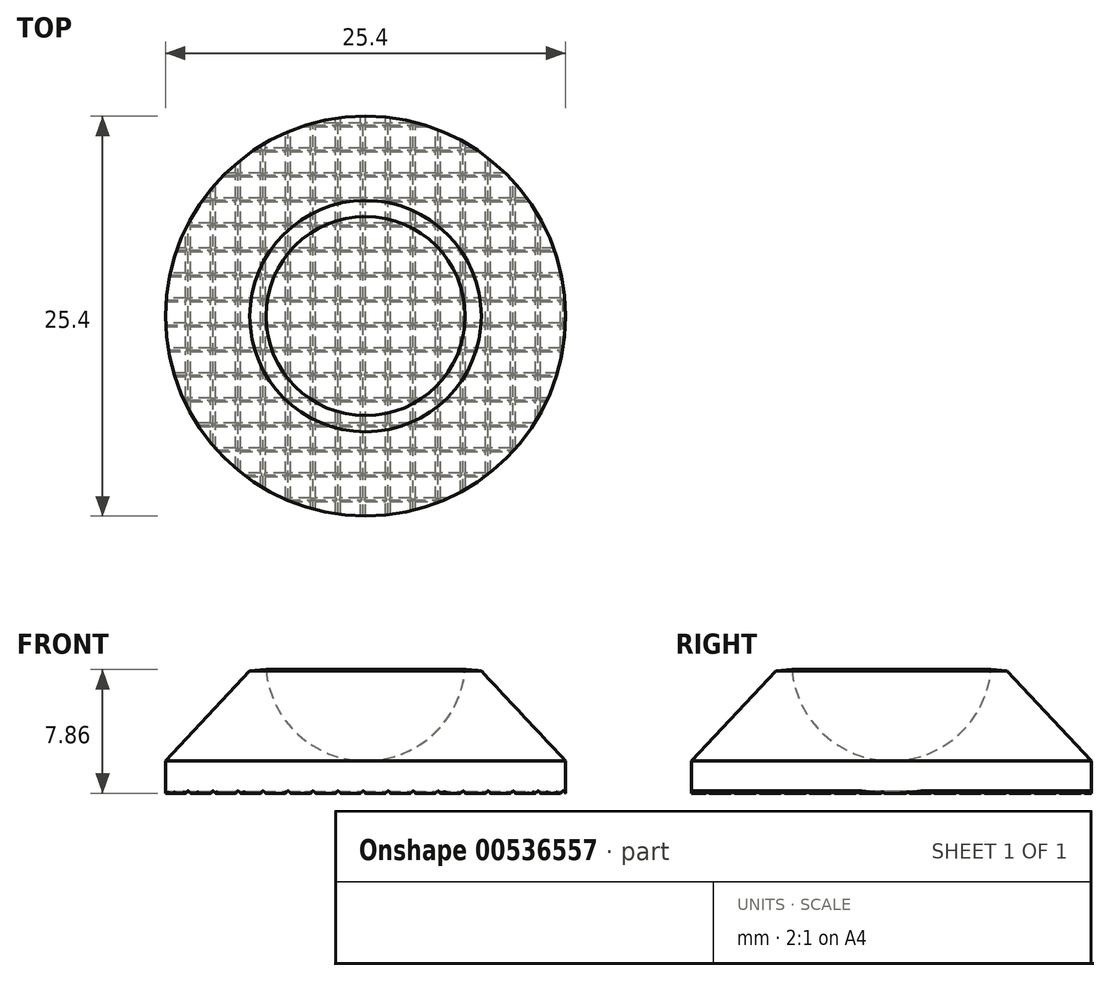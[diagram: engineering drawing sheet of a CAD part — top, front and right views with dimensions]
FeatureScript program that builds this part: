
annotation { "Feature Type Name" : "Feature", "Feature Type Description" : "" }
export const myFeature = defineFeature(function(context is Context, id is Id, definition is map)
    precondition{}
    {
        {
            var Q0;
            Q0=qCreatedBy(makeId("Front.planeOp"),FACE);
            var sketch = newSketch(context, id + "F0", { "sketchPlane" : qUnion([Q0])});
            skLineSegment(sketch, "E0", {"start": v(0, 0) * mm, "end": v(12.7, 0) * mm});
            skLineSegment(sketch, "E1", {"start": v(12.7, 0) * mm, "end": v(12.7, 2.06) * mm});
            skLineSegment(sketch, "E2", {"start": v(12.7, 2.06) * mm, "end": v(6.75, 8.41) * mm, "construction": true});
            skLineSegment(sketch, "E3", {"start": v(6.75, 8.41) * mm, "end": v(6.35, 8.41) * mm});
            skLineSegment(sketch, "E4", {"start": v(0, 0) * mm, "end": v(0, 2.06) * mm});
            skLineSegment(sketch, "E5", {"start": v(6.35, 8.41) * mm, "end": v(0, 8.41) * mm, "construction": true});
            skLineSegment(sketch, "E6", {"start": v(0, 8.41) * mm, "end": v(0, 2.06) * mm, "construction": true});
            skArc(sketch, "E7", {"start": v(0, 2.06) * mm, "mid": v(4.5, 3.92) * mm, "end": v(6.35, 8.41) * mm, "construction": true});
            skLineSegment(sketch, "E8", {"start": v(0, 2.06) * mm, "end": v(12.7, 2.06) * mm, "construction": true});
            skLineSegment(sketch, "E9", {"start": v(0, 8.41) * mm, "end": v(7.35, 7.77) * mm, "construction": true});
            skLineSegment(sketch, "E10", {"start": v(7.35, 7.77) * mm, "end": v(12.7, 2.06) * mm});
            skArc(sketch, "E11", {"start": v(0, 2.06) * mm, "mid": v(4.29, 3.73) * mm, "end": v(6.33, 7.86) * mm});
            skLineSegment(sketch, "E12", {"start": v(7.35, 7.77) * mm, "end": v(6.33, 7.86) * mm});
            skSolve(sketch);
        }
        {
            var Q0;
            Q0=qSketchRegion(id+"F0",true);
            var Q1;
            Q1=sQuery(id+"F0.wireOp",EDGE,"E6");
            revolve(context, id + "F1", {"entities" : qUnion([Q0]), "axis" : qUnion([Q1]), "revolveType" : RevolveType.FULL});
        }
        {
            var Q0;
            Q0=qCreatedBy(makeId("Front.planeOp"),FACE);
            var sketch = newSketch(context, id + "F2", { "sketchPlane" : qUnion([Q0])});
            skLineSegment(sketch, "E13", {"start": v(-12.7, 0) * mm, "end": v(-12.86, 0.16) * mm});
            skLineSegment(sketch, "E14", {"start": v(-12.86, 0.16) * mm, "end": v(-13.02, 0) * mm});
            skLineSegment(sketch, "E15", {"start": v(-13.02, 0) * mm, "end": v(-12.7, 0) * mm});
            skLineSegment(sketch, "E16.1.0.0", {"start": v(-11.11, 0) * mm, "end": v(-11.27, 0.16) * mm});
            skLineSegment(sketch, "E16.1.0.1", {"start": v(-11.27, 0.16) * mm, "end": v(-11.43, 0) * mm});
            skLineSegment(sketch, "E16.1.0.2", {"start": v(-11.43, 0) * mm, "end": v(-11.11, 0) * mm});
            skLineSegment(sketch, "E16.2.0.0", {"start": v(-9.53, 0) * mm, "end": v(-9.68, 0.16) * mm});
            skLineSegment(sketch, "E16.2.0.1", {"start": v(-9.68, 0.16) * mm, "end": v(-9.84, 0) * mm});
            skLineSegment(sketch, "E16.2.0.2", {"start": v(-9.84, 0) * mm, "end": v(-9.53, 0) * mm});
            skLineSegment(sketch, "E16.3.0.0", {"start": v(-7.94, 0) * mm, "end": v(-8.1, 0.16) * mm});
            skLineSegment(sketch, "E16.3.0.1", {"start": v(-8.1, 0.16) * mm, "end": v(-8.26, 0) * mm});
            skLineSegment(sketch, "E16.3.0.2", {"start": v(-8.26, 0) * mm, "end": v(-7.94, 0) * mm});
            skLineSegment(sketch, "E16.4.0.0", {"start": v(-6.35, 0) * mm, "end": v(-6.5, 0.16) * mm});
            skLineSegment(sketch, "E16.4.0.1", {"start": v(-6.5, 0.16) * mm, "end": v(-6.67, 0) * mm});
            skLineSegment(sketch, "E16.4.0.2", {"start": v(-6.67, 0) * mm, "end": v(-6.35, 0) * mm});
            skLineSegment(sketch, "E16.5.0.0", {"start": v(-4.76, 0) * mm, "end": v(-4.92, 0.16) * mm});
            skLineSegment(sketch, "E16.5.0.1", {"start": v(-4.92, 0.16) * mm, "end": v(-5.08, 0) * mm});
            skLineSegment(sketch, "E16.5.0.2", {"start": v(-5.08, 0) * mm, "end": v(-4.76, 0) * mm});
            skLineSegment(sketch, "E16.6.0.0", {"start": v(-3.18, 0) * mm, "end": v(-3.33, 0.16) * mm});
            skLineSegment(sketch, "E16.6.0.1", {"start": v(-3.33, 0.16) * mm, "end": v(-3.5, 0) * mm});
            skLineSegment(sketch, "E16.6.0.2", {"start": v(-3.5, 0) * mm, "end": v(-3.18, 0) * mm});
            skLineSegment(sketch, "E16.7.0.0", {"start": v(-1.59, 0) * mm, "end": v(-1.75, 0.16) * mm});
            skLineSegment(sketch, "E16.7.0.1", {"start": v(-1.75, 0.16) * mm, "end": v(-1.9, 0) * mm});
            skLineSegment(sketch, "E16.7.0.2", {"start": v(-1.9, 0) * mm, "end": v(-1.59, 0) * mm});
            skLineSegment(sketch, "E16.8.0.0", {"start": v(0, 0) * mm, "end": v(-0.16, 0.16) * mm});
            skLineSegment(sketch, "E16.8.0.1", {"start": v(-0.16, 0.16) * mm, "end": v(-0.32, 0) * mm});
            skLineSegment(sketch, "E16.8.0.2", {"start": v(-0.32, 0) * mm, "end": v(0, 0) * mm});
            skLineSegment(sketch, "E16.9.0.0", {"start": v(1.59, 0) * mm, "end": v(1.43, 0.16) * mm});
            skLineSegment(sketch, "E16.9.0.1", {"start": v(1.43, 0.16) * mm, "end": v(1.27, 0) * mm});
            skLineSegment(sketch, "E16.9.0.2", {"start": v(1.27, 0) * mm, "end": v(1.59, 0) * mm});
            skLineSegment(sketch, "E16.10.0.0", {"start": v(3.17, 0) * mm, "end": v(3.02, 0.16) * mm});
            skLineSegment(sketch, "E16.10.0.1", {"start": v(3.02, 0.16) * mm, "end": v(2.86, 0) * mm});
            skLineSegment(sketch, "E16.10.0.2", {"start": v(2.86, 0) * mm, "end": v(3.17, 0) * mm});
            skLineSegment(sketch, "E16.11.0.0", {"start": v(4.76, 0) * mm, "end": v(4.6, 0.16) * mm});
            skLineSegment(sketch, "E16.11.0.1", {"start": v(4.6, 0.16) * mm, "end": v(4.44, 0) * mm});
            skLineSegment(sketch, "E16.11.0.2", {"start": v(4.44, 0) * mm, "end": v(4.76, 0) * mm});
            skLineSegment(sketch, "E16.12.0.0", {"start": v(6.35, 0) * mm, "end": v(6.2, 0.16) * mm});
            skLineSegment(sketch, "E16.12.0.1", {"start": v(6.2, 0.16) * mm, "end": v(6.03, 0) * mm});
            skLineSegment(sketch, "E16.12.0.2", {"start": v(6.03, 0) * mm, "end": v(6.35, 0) * mm});
            skLineSegment(sketch, "E16.13.0.0", {"start": v(7.94, 0) * mm, "end": v(7.78, 0.16) * mm});
            skLineSegment(sketch, "E16.13.0.1", {"start": v(7.78, 0.16) * mm, "end": v(7.62, 0) * mm});
            skLineSegment(sketch, "E16.13.0.2", {"start": v(7.62, 0) * mm, "end": v(7.94, 0) * mm});
            skLineSegment(sketch, "E16.14.0.0", {"start": v(9.52, 0) * mm, "end": v(9.37, 0.16) * mm});
            skLineSegment(sketch, "E16.14.0.1", {"start": v(9.37, 0.16) * mm, "end": v(9.2, 0) * mm});
            skLineSegment(sketch, "E16.14.0.2", {"start": v(9.2, 0) * mm, "end": v(9.52, 0) * mm});
            skLineSegment(sketch, "E16.15.0.0", {"start": v(11.11, 0) * mm, "end": v(10.95, 0.16) * mm});
            skLineSegment(sketch, "E16.15.0.1", {"start": v(10.95, 0.16) * mm, "end": v(10.8, 0) * mm});
            skLineSegment(sketch, "E16.15.0.2", {"start": v(10.8, 0) * mm, "end": v(11.11, 0) * mm});
            skLineSegment(sketch, "E16.16.0.0", {"start": v(12.7, 0) * mm, "end": v(12.54, 0.16) * mm});
            skLineSegment(sketch, "E16.16.0.1", {"start": v(12.54, 0.16) * mm, "end": v(12.38, 0) * mm});
            skLineSegment(sketch, "E16.16.0.2", {"start": v(12.38, 0) * mm, "end": v(12.7, 0) * mm});
            skLineSegment(sketch, "E16.17.0.0", {"start": v(14.29, 0) * mm, "end": v(14.13, 0.16) * mm});
            skLineSegment(sketch, "E16.17.0.1", {"start": v(14.13, 0.16) * mm, "end": v(13.97, 0) * mm});
            skLineSegment(sketch, "E16.17.0.2", {"start": v(13.97, 0) * mm, "end": v(14.29, 0) * mm});
            skLineSegment(sketch, "E16.18.0.0", {"start": v(15.87, 0) * mm, "end": v(15.72, 0.16) * mm});
            skLineSegment(sketch, "E16.18.0.1", {"start": v(15.72, 0.16) * mm, "end": v(15.56, 0) * mm});
            skLineSegment(sketch, "E16.18.0.2", {"start": v(15.56, 0) * mm, "end": v(15.87, 0) * mm});
            skLineSegment(sketch, "E16.19.0.0", {"start": v(17.46, 0) * mm, "end": v(17.3, 0.16) * mm});
            skLineSegment(sketch, "E16.19.0.1", {"start": v(17.3, 0.16) * mm, "end": v(17.14, 0) * mm});
            skLineSegment(sketch, "E16.19.0.2", {"start": v(17.14, 0) * mm, "end": v(17.46, 0) * mm});
            skLineSegment(sketch, "E16.direction1", {"start": v(-13.02, 0) * mm, "end": v(-11.43, 0) * mm, "construction": true});
            skSolve(sketch);
        }
        {
            var Q0;
            Q0=qSketchRegion(id+"F2",true);
            extrude(context, id + "F3", {"entities" : qUnion([Q0]), "operationType" : NewBodyOperationType.REMOVE, "endBound" : BoundingType.SYMMETRIC, "depth" : 25.4 * mm, "offsetDistance" : 25.4 * mm});
        }
        {
            var Q0;
            Q0=qCreatedBy(makeId("Right.planeOp"),FACE);
            var sketch = newSketch(context, id + "F4", { "sketchPlane" : qUnion([Q0])});
            skLineSegment(sketch, "E17", {"start": v(-14.69, -0.05) * mm, "end": v(-14.84, 0.1) * mm});
            skLineSegment(sketch, "E18", {"start": v(-14.84, 0.1) * mm, "end": v(-15, -0.05) * mm});
            skLineSegment(sketch, "E19", {"start": v(-15, -0.05) * mm, "end": v(-14.69, -0.05) * mm});
            skLineSegment(sketch, "E20.1.0.0", {"start": v(-13.1, -0.05) * mm, "end": v(-13.26, 0.1) * mm});
            skLineSegment(sketch, "E20.1.0.1", {"start": v(-13.26, 0.1) * mm, "end": v(-13.42, -0.05) * mm});
            skLineSegment(sketch, "E20.1.0.2", {"start": v(-13.42, -0.05) * mm, "end": v(-13.1, -0.05) * mm});
            skLineSegment(sketch, "E20.2.0.0", {"start": v(-11.51, -0.05) * mm, "end": v(-11.67, 0.1) * mm});
            skLineSegment(sketch, "E20.2.0.1", {"start": v(-11.67, 0.1) * mm, "end": v(-11.83, -0.05) * mm});
            skLineSegment(sketch, "E20.2.0.2", {"start": v(-11.83, -0.05) * mm, "end": v(-11.51, -0.05) * mm});
            skLineSegment(sketch, "E20.3.0.0", {"start": v(-9.92, -0.05) * mm, "end": v(-10.08, 0.1) * mm});
            skLineSegment(sketch, "E20.3.0.1", {"start": v(-10.08, 0.1) * mm, "end": v(-10.24, -0.05) * mm});
            skLineSegment(sketch, "E20.3.0.2", {"start": v(-10.24, -0.05) * mm, "end": v(-9.92, -0.05) * mm});
            skLineSegment(sketch, "E20.4.0.0", {"start": v(-8.34, -0.05) * mm, "end": v(-8.5, 0.1) * mm});
            skLineSegment(sketch, "E20.4.0.1", {"start": v(-8.5, 0.1) * mm, "end": v(-8.65, -0.05) * mm});
            skLineSegment(sketch, "E20.4.0.2", {"start": v(-8.65, -0.05) * mm, "end": v(-8.34, -0.05) * mm});
            skLineSegment(sketch, "E20.5.0.0", {"start": v(-6.75, -0.05) * mm, "end": v(-6.9, 0.1) * mm});
            skLineSegment(sketch, "E20.5.0.1", {"start": v(-6.9, 0.1) * mm, "end": v(-7.07, -0.05) * mm});
            skLineSegment(sketch, "E20.5.0.2", {"start": v(-7.07, -0.05) * mm, "end": v(-6.75, -0.05) * mm});
            skLineSegment(sketch, "E20.6.0.0", {"start": v(-5.16, -0.05) * mm, "end": v(-5.32, 0.1) * mm});
            skLineSegment(sketch, "E20.6.0.1", {"start": v(-5.32, 0.1) * mm, "end": v(-5.48, -0.05) * mm});
            skLineSegment(sketch, "E20.6.0.2", {"start": v(-5.48, -0.05) * mm, "end": v(-5.16, -0.05) * mm});
            skLineSegment(sketch, "E20.7.0.0", {"start": v(-3.57, -0.05) * mm, "end": v(-3.73, 0.1) * mm});
            skLineSegment(sketch, "E20.7.0.1", {"start": v(-3.73, 0.1) * mm, "end": v(-3.9, -0.05) * mm});
            skLineSegment(sketch, "E20.7.0.2", {"start": v(-3.9, -0.05) * mm, "end": v(-3.57, -0.05) * mm});
            skLineSegment(sketch, "E20.8.0.0", {"start": v(-1.99, -0.05) * mm, "end": v(-2.14, 0.1) * mm});
            skLineSegment(sketch, "E20.8.0.1", {"start": v(-2.14, 0.1) * mm, "end": v(-2.3, -0.05) * mm});
            skLineSegment(sketch, "E20.8.0.2", {"start": v(-2.3, -0.05) * mm, "end": v(-1.99, -0.05) * mm});
            skLineSegment(sketch, "E20.9.0.0", {"start": v(-0.4, -0.05) * mm, "end": v(-0.56, 0.1) * mm});
            skLineSegment(sketch, "E20.9.0.1", {"start": v(-0.56, 0.1) * mm, "end": v(-0.72, -0.05) * mm});
            skLineSegment(sketch, "E20.9.0.2", {"start": v(-0.72, -0.05) * mm, "end": v(-0.4, -0.05) * mm});
            skLineSegment(sketch, "E20.10.0.0", {"start": v(1.19, -0.05) * mm, "end": v(1.03, 0.1) * mm});
            skLineSegment(sketch, "E20.10.0.1", {"start": v(1.03, 0.1) * mm, "end": v(0.87, -0.05) * mm});
            skLineSegment(sketch, "E20.10.0.2", {"start": v(0.87, -0.05) * mm, "end": v(1.19, -0.05) * mm});
            skLineSegment(sketch, "E20.11.0.0", {"start": v(2.78, -0.05) * mm, "end": v(2.62, 0.1) * mm});
            skLineSegment(sketch, "E20.11.0.1", {"start": v(2.62, 0.1) * mm, "end": v(2.46, -0.05) * mm});
            skLineSegment(sketch, "E20.11.0.2", {"start": v(2.46, -0.05) * mm, "end": v(2.78, -0.05) * mm});
            skLineSegment(sketch, "E20.12.0.0", {"start": v(4.36, -0.05) * mm, "end": v(4.2, 0.1) * mm});
            skLineSegment(sketch, "E20.12.0.1", {"start": v(4.2, 0.1) * mm, "end": v(4.05, -0.05) * mm});
            skLineSegment(sketch, "E20.12.0.2", {"start": v(4.05, -0.05) * mm, "end": v(4.36, -0.05) * mm});
            skLineSegment(sketch, "E20.13.0.0", {"start": v(5.95, -0.05) * mm, "end": v(5.8, 0.1) * mm});
            skLineSegment(sketch, "E20.13.0.1", {"start": v(5.8, 0.1) * mm, "end": v(5.63, -0.05) * mm});
            skLineSegment(sketch, "E20.13.0.2", {"start": v(5.63, -0.05) * mm, "end": v(5.95, -0.05) * mm});
            skLineSegment(sketch, "E20.14.0.0", {"start": v(7.54, -0.05) * mm, "end": v(7.38, 0.1) * mm});
            skLineSegment(sketch, "E20.14.0.1", {"start": v(7.38, 0.1) * mm, "end": v(7.22, -0.05) * mm});
            skLineSegment(sketch, "E20.14.0.2", {"start": v(7.22, -0.05) * mm, "end": v(7.54, -0.05) * mm});
            skLineSegment(sketch, "E20.15.0.0", {"start": v(9.13, -0.05) * mm, "end": v(8.97, 0.1) * mm});
            skLineSegment(sketch, "E20.15.0.1", {"start": v(8.97, 0.1) * mm, "end": v(8.8, -0.05) * mm});
            skLineSegment(sketch, "E20.15.0.2", {"start": v(8.8, -0.05) * mm, "end": v(9.13, -0.05) * mm});
            skLineSegment(sketch, "E20.16.0.0", {"start": v(10.71, -0.05) * mm, "end": v(10.56, 0.1) * mm});
            skLineSegment(sketch, "E20.16.0.1", {"start": v(10.56, 0.1) * mm, "end": v(10.4, -0.05) * mm});
            skLineSegment(sketch, "E20.16.0.2", {"start": v(10.4, -0.05) * mm, "end": v(10.71, -0.05) * mm});
            skLineSegment(sketch, "E20.17.0.0", {"start": v(12.3, -0.05) * mm, "end": v(12.14, 0.1) * mm});
            skLineSegment(sketch, "E20.17.0.1", {"start": v(12.14, 0.1) * mm, "end": v(11.98, -0.05) * mm});
            skLineSegment(sketch, "E20.17.0.2", {"start": v(11.98, -0.05) * mm, "end": v(12.3, -0.05) * mm});
            skLineSegment(sketch, "E20.18.0.0", {"start": v(13.89, -0.05) * mm, "end": v(13.73, 0.1) * mm});
            skLineSegment(sketch, "E20.18.0.1", {"start": v(13.73, 0.1) * mm, "end": v(13.57, -0.05) * mm});
            skLineSegment(sketch, "E20.18.0.2", {"start": v(13.57, -0.05) * mm, "end": v(13.89, -0.05) * mm});
            skLineSegment(sketch, "E20.19.0.0", {"start": v(15.48, -0.05) * mm, "end": v(15.32, 0.1) * mm});
            skLineSegment(sketch, "E20.19.0.1", {"start": v(15.32, 0.1) * mm, "end": v(15.16, -0.05) * mm});
            skLineSegment(sketch, "E20.19.0.2", {"start": v(15.16, -0.05) * mm, "end": v(15.48, -0.05) * mm});
            skLineSegment(sketch, "E20.direction1", {"start": v(-15, -0.05) * mm, "end": v(-13.42, -0.05) * mm, "construction": true});
            skSolve(sketch);
        }
        {
            var Q0;
            Q0=qSketchRegion(id+"F4",true);
            extrude(context, id + "F5", {"entities" : qUnion([Q0]), "operationType" : NewBodyOperationType.REMOVE, "endBound" : BoundingType.SYMMETRIC, "oppositeDirection" : true, "depth" : 25.4 * mm, "offsetDistance" : 25.4 * mm});
        }
    });
